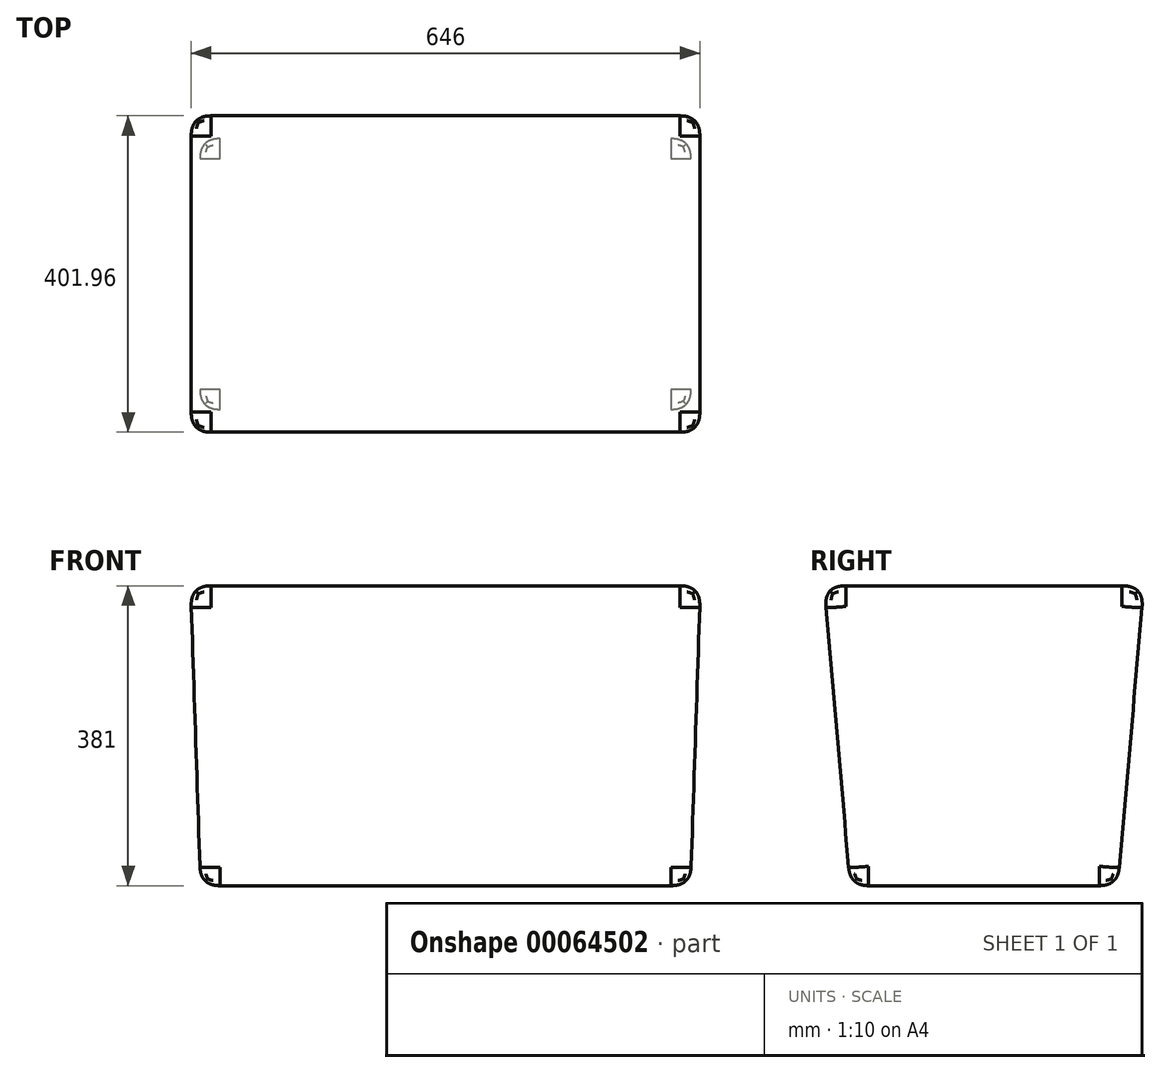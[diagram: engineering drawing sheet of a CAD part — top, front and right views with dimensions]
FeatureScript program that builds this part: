
annotation { "Feature Type Name" : "Feature", "Feature Type Description" : "" }
export const myFeature = defineFeature(function(context is Context, id is Id, definition is map)
    precondition{}
    {
        {
            var Q0;
            Q0=qCreatedBy(makeId("Top.planeOp"),FACE);
            var sketch = newSketch(context, id + "F0", { "sketchPlane" : qUnion([Q0])});
            skLineSegment(sketch, "E0.rect.bottom", {"start": v(311.15, -169.86) * mm, "end": v(-311.15, -169.86) * mm});
            skLineSegment(sketch, "E0.rect.top", {"start": v(311.15, 169.86) * mm, "end": v(-311.15, 169.86) * mm});
            skLineSegment(sketch, "E0.rect.left", {"start": v(311.15, -169.86) * mm, "end": v(311.15, 169.86) * mm});
            skLineSegment(sketch, "E0.rect.right", {"start": v(-311.15, -169.86) * mm, "end": v(-311.15, 169.86) * mm});
            skPoint(sketch, "E0.rect.middle", {"position": v(0, 0) * mm});
            skSolve(sketch);
        }
        {
            var Q0;
            Q0=makeQuery(id+"F0.imprint","IMPRINT",FACE,{"disambiguationData":[TD([[makeQuery(id+"F0.imprint","IMPRINT",EDGE,{"derivedFrom":sQuery(id+"F0.wireOp",EDGE,"E0.rect.bottom")}),-1.0]])]});
            cPlane(context, id + "F1", {"entities" : qUnion([Q0]), "cplaneType" : CPlaneType.OFFSET, "offset" : 381 * mm, "width" : 152.4 * mm, "height" : 152.4 * mm});
        }
        {
            var Q0;
            Q0=qCreatedBy(id+"F1.planeOp",FACE);
            var sketch = newSketch(context, id + "F2", { "sketchPlane" : qUnion([Q0])});
            skLineSegment(sketch, "E1.rect.bottom", {"start": v(323.85, -203.2) * mm, "end": v(-323.85, -203.2) * mm});
            skLineSegment(sketch, "E1.rect.top", {"start": v(323.85, 203.2) * mm, "end": v(-323.85, 203.2) * mm});
            skLineSegment(sketch, "E1.rect.left", {"start": v(323.85, -203.2) * mm, "end": v(323.85, 203.2) * mm});
            skLineSegment(sketch, "E1.rect.right", {"start": v(-323.85, -203.2) * mm, "end": v(-323.85, 203.2) * mm});
            skPoint(sketch, "E1.rect.middle", {"position": v(0, 0) * mm});
            skSolve(sketch);
        }
        {
            var Q0;
            Q0=makeQuery(id+"F0.imprint","IMPRINT",FACE,{"disambiguationData":[TD([[makeQuery(id+"F0.imprint","IMPRINT",EDGE,{"derivedFrom":sQuery(id+"F0.wireOp",EDGE,"E0.rect.bottom")}),-1.0]])]});
            var Q1;
            Q1=makeQuery(id+"F2.imprint","IMPRINT",FACE,{"disambiguationData":[TD([[makeQuery(id+"F2.imprint","IMPRINT",EDGE,{"derivedFrom":sQuery(id+"F2.wireOp",EDGE,"E1.rect.bottom")}),-1.0]])]});
            loft(context, id + "F3", {"sheetProfilesArray" : [{ "sheetProfileEntities" : qUnion([Q0]) }, { "sheetProfileEntities" : qUnion([Q1]) }]});
        }
        {
            var Q0;
            Q0=makeQuery(id+"F3.opLoft","SWEPT_FACE",FACE,{"disambiguationData":[OSD([sQuery(id+"F0.wireOp",EDGE,"E0.rect.bottom"),sQuery(id+"F0.wireOp",EDGE,"E0.rect.top"),sQuery(id+"F0.wireOp",EDGE,"E0.rect.left"),sQuery(id+"F2.wireOp",EDGE,"E1.rect.bottom"),sQuery(id+"F2.wireOp",EDGE,"E1.rect.top"),sQuery(id+"F2.wireOp",EDGE,"E1.rect.left")])]});
            var Q1;
            Q1=makeQuery(id+"F3.opLoft","SWEPT_FACE",FACE,{"disambiguationData":[OSD([sQuery(id+"F0.wireOp",EDGE,"E0.rect.bottom"),sQuery(id+"F0.wireOp",EDGE,"E0.rect.top"),sQuery(id+"F0.wireOp",EDGE,"E0.rect.right"),sQuery(id+"F2.wireOp",EDGE,"E1.rect.bottom"),sQuery(id+"F2.wireOp",EDGE,"E1.rect.top"),sQuery(id+"F2.wireOp",EDGE,"E1.rect.right")])]});
            var Q2;
            Q2=makeQuery(id+"F3.opLoft","SWEPT_FACE",FACE,{"disambiguationData":[OSD([sQuery(id+"F0.wireOp",EDGE,"E0.rect.bottom"),sQuery(id+"F0.wireOp",EDGE,"E0.rect.left"),sQuery(id+"F0.wireOp",EDGE,"E0.rect.right"),sQuery(id+"F2.wireOp",EDGE,"E1.rect.bottom"),sQuery(id+"F2.wireOp",EDGE,"E1.rect.left"),sQuery(id+"F2.wireOp",EDGE,"E1.rect.right")])]});
            var Q3;
            Q3=makeQuery(id+"F3.opLoft","SWEPT_FACE",FACE,{"disambiguationData":[OSD([sQuery(id+"F0.wireOp",EDGE,"E0.rect.top"),sQuery(id+"F0.wireOp",EDGE,"E0.rect.left"),sQuery(id+"F0.wireOp",EDGE,"E0.rect.right"),sQuery(id+"F2.wireOp",EDGE,"E1.rect.top"),sQuery(id+"F2.wireOp",EDGE,"E1.rect.left"),sQuery(id+"F2.wireOp",EDGE,"E1.rect.right")])]});
            fillet(context, id + "F4", {"entities" : qUnion([Q0, Q1, Q2, Q3]), "radius" : 25.4 * mm, "tangentPropagation" : true, "rho" : 0.5, "crossSection" : FilletCrossSection.CONIC, "allowEdgeOverflow" : false});
        }
    });
